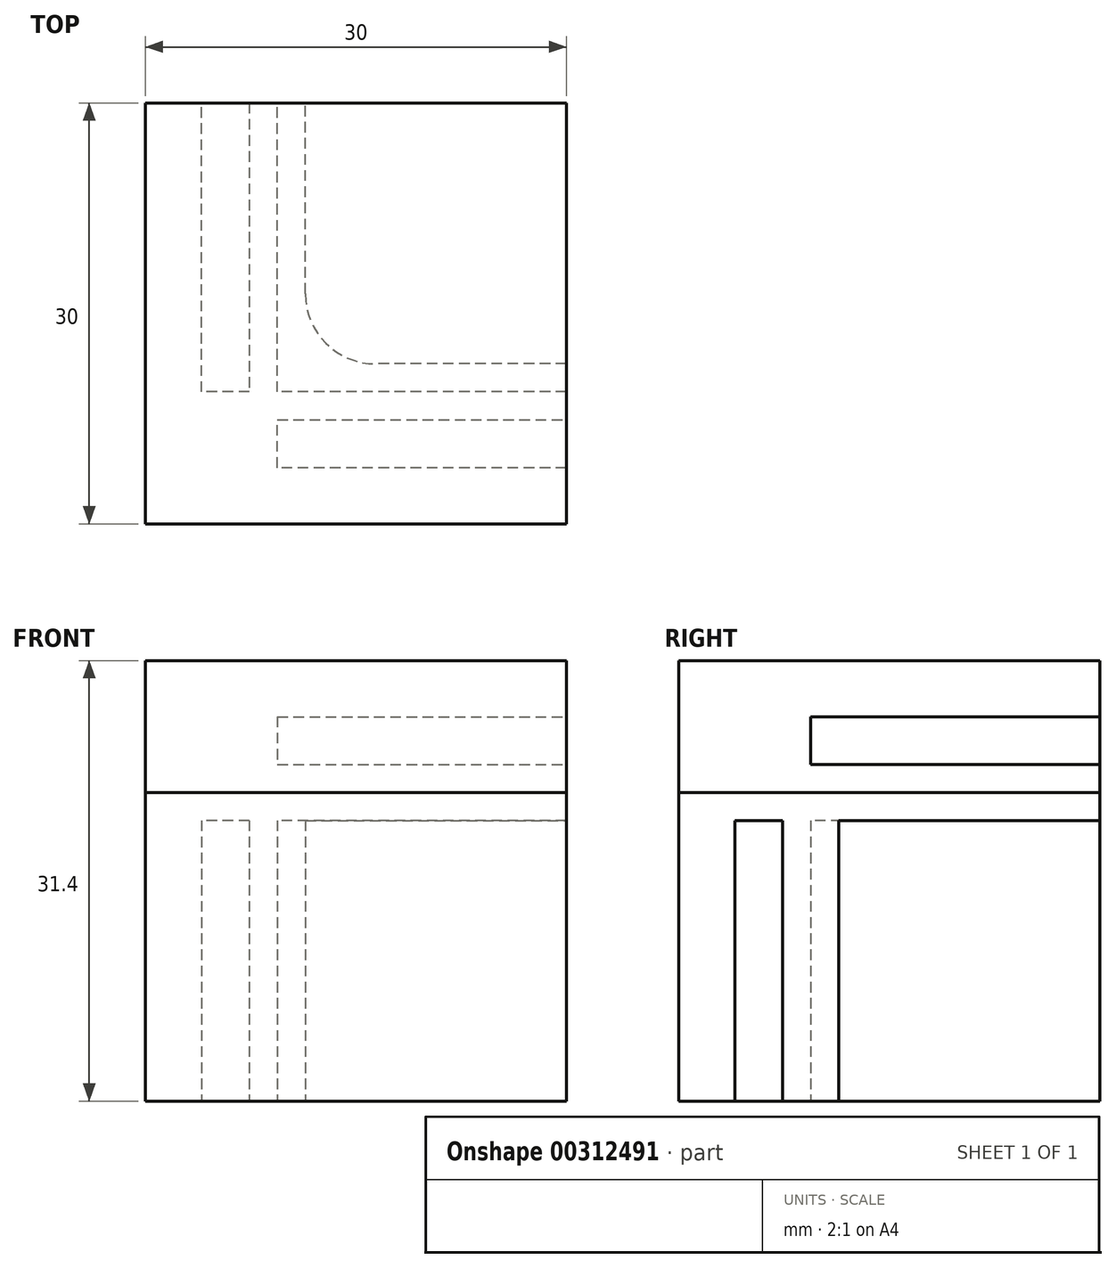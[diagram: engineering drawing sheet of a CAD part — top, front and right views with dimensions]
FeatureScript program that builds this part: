
annotation { "Feature Type Name" : "Feature", "Feature Type Description" : "" }
export const myFeature = defineFeature(function(context is Context, id is Id, definition is map)
    precondition{}
    {
        {
            assignVariable(context, id + "F0", {"name" : "a", "anyValue" : 4});
        }
        {
            assignVariable(context, id + "F1", {"name" : "b", "anyValue" : 3.4});
        }
        {
            assignVariable(context, id + "F2", {"name" : "h", "anyValue" : 30});
        }
        {
            var Q0;
            Q0=qCreatedBy(makeId("Top.planeOp"),FACE);
            var sketch = newSketch(context, id + "F3", { "sketchPlane" : qUnion([Q0])});
            skLineSegment(sketch, "E0", {"start": v(-4, 18.6) * mm, "end": v(-4, -2) * mm});
            skLineSegment(sketch, "E1", {"start": v(-4, -2) * mm, "end": v(-7.4, -2) * mm});
            skLineSegment(sketch, "E2", {"start": v(-7.4, -2) * mm, "end": v(-7.4, 18.6) * mm});
            skLineSegment(sketch, "E3", {"start": v(-7.4, 18.6) * mm, "end": v(-11.4, 18.6) * mm});
            skLineSegment(sketch, "E4", {"start": v(-11.4, 18.6) * mm, "end": v(-11.4, -11.4) * mm});
            skLineSegment(sketch, "E5", {"start": v(-11.4, -11.4) * mm, "end": v(18.6, -11.4) * mm});
            skLineSegment(sketch, "E6", {"start": v(18.6, -11.4) * mm, "end": v(18.6, -7.4) * mm});
            skLineSegment(sketch, "E7", {"start": v(18.6, -7.4) * mm, "end": v(-2, -7.4) * mm});
            skLineSegment(sketch, "E8", {"start": v(-2, -7.4) * mm, "end": v(-2, -4) * mm});
            skLineSegment(sketch, "E9", {"start": v(-2, -4) * mm, "end": v(18.6, -4) * mm});
            skLineSegment(sketch, "E10", {"start": v(18.6, -4) * mm, "end": v(18.6, 0) * mm});
            skLineSegment(sketch, "E11", {"start": v(18.6, 0) * mm, "end": v(0, 0) * mm});
            skLineSegment(sketch, "E12", {"start": v(0, 0) * mm, "end": v(0, 18.6) * mm});
            skLineSegment(sketch, "E13", {"start": v(0, 18.6) * mm, "end": v(-4, 18.6) * mm});
            skLineSegment(sketch, "E14", {"start": v(-4, -2) * mm, "end": v(-2, -2) * mm, "construction": true});
            skLineSegment(sketch, "E15", {"start": v(-2, -4) * mm, "end": v(-2, -2) * mm, "construction": true});
            skSolve(sketch);
        }
        {
            var Q0;
            Q0=makeQuery(id+"F3.imprint","IMPRINT",FACE,{"disambiguationData":[TD([[makeQuery(id+"F3.imprint","IMPRINT",EDGE,{"derivedFrom":sQuery(id+"F3.wireOp",EDGE,"E0")}),1.0]])]});
            extrude(context, id + "F4", {"entities" : qUnion([Q0]), "depth" : (getVariable(context, 'h') - 10) * mm});
        }
        {
            var Q0;
            Q0=makeQuery(id+"F4.opExtrude","CAP_FACE",FACE,{"disambiguationData":[OSD([sQuery(id+"F3.wireOp",EDGE,"E0"),sQuery(id+"F3.wireOp",EDGE,"E1"),sQuery(id+"F3.wireOp",EDGE,"E2"),sQuery(id+"F3.wireOp",EDGE,"E3"),sQuery(id+"F3.wireOp",EDGE,"E4"),sQuery(id+"F3.wireOp",EDGE,"E5"),sQuery(id+"F3.wireOp",EDGE,"E6"),sQuery(id+"F3.wireOp",EDGE,"E7"),sQuery(id+"F3.wireOp",EDGE,"E8"),sQuery(id+"F3.wireOp",EDGE,"E9"),sQuery(id+"F3.wireOp",EDGE,"E10"),sQuery(id+"F3.wireOp",EDGE,"E11"),sQuery(id+"F3.wireOp",EDGE,"E12"),sQuery(id+"F3.wireOp",EDGE,"E13")])],"isStart":false});
            var sketch = newSketch(context, id + "F5", { "sketchPlane" : qUnion([Q0])});
            skLineSegment(sketch, "E16.bottom", {"start": v(-11.4, -11.4) * mm, "end": v(18.6, -11.4) * mm});
            skLineSegment(sketch, "E16.top", {"start": v(-11.4, 18.6) * mm, "end": v(18.6, 18.6) * mm});
            skLineSegment(sketch, "E16.left", {"start": v(-11.4, -11.4) * mm, "end": v(-11.4, 18.6) * mm});
            skLineSegment(sketch, "E16.right", {"start": v(18.6, -11.4) * mm, "end": v(18.6, 18.6) * mm});
            skSolve(sketch);
        }
        {
            var Q0;
            {var subQ1=makeQuery(id+"F4.opExtrude","CAP_EDGE",EDGE,{"disambiguationData":[OSD([sQuery(id+"F3.wireOp",EDGE,"E0")])],"isStart":false});Q0=makeQuery(id+"F5.imprint","IMPRINT",FACE,{"disambiguationData":[TD([[makeQuery(id+"F5.imprint","IMPRINT",EDGE,{"derivedFrom":subQ1}),-1.0]])]});}
            var Q1;
            {var subQ4=sQuery(id+"F5.wireOp",EDGE,"E16.bottom");Q1=makeQuery(id+"F5.imprint","IMPRINT",FACE,{"disambiguationData":[TD([[makeQuery(id+"F5.imprint","IMPRINT",EDGE,{"derivedFrom":subQ4}),1.0]])]});}
            var Q2;
            {var subQ1=makeQuery(id+"F4.opExtrude","CAP_EDGE",EDGE,{"disambiguationData":[OSD([sQuery(id+"F3.wireOp",EDGE,"E7")])],"isStart":false});Q2=makeQuery(id+"F5.imprint","IMPRINT",FACE,{"disambiguationData":[TD([[makeQuery(id+"F5.imprint","IMPRINT",EDGE,{"derivedFrom":subQ1}),-1.0]])]});}
            var Q3;
            {var subQ4=makeQuery(id+"F4.opExtrude","CAP_EDGE",EDGE,{"disambiguationData":[OSD([sQuery(id+"F3.wireOp",EDGE,"E11")])],"isStart":false});Q3=makeQuery(id+"F5.imprint","IMPRINT",FACE,{"disambiguationData":[TD([[makeQuery(id+"F5.imprint","IMPRINT",EDGE,{"derivedFrom":subQ4}),-1.0]])]});}
            extrude(context, id + "F6", {"entities" : qUnion([Q0, Q1, Q2, Q3]), "operationType" : NewBodyOperationType.ADD, "depth" : (getVariable(context, 'a') / 2) * mm});
        }
        {
            var Q0;
            Q0=makeQuery(id+"F6.opExtrude","CAP_FACE",FACE,{"disambiguationData":[OSD([sQuery(id+"F5.wireOp",EDGE,"E16.bottom"),sQuery(id+"F5.wireOp",EDGE,"E16.top"),sQuery(id+"F5.wireOp",EDGE,"E16.left"),sQuery(id+"F5.wireOp",EDGE,"E16.right")])],"isStart":false});
            extrude(context, id + "F7", {"entities" : qUnion([Q0]), "depth" : (getVariable(context, 'a') / 2) * mm});
        }
        {
            var Q0;
            Q0=makeQuery(id+"F7.opExtrude","CAP_FACE",FACE,{"disambiguationData":[OSD([sQuery(id+"F5.wireOp",EDGE,"E16.bottom"),sQuery(id+"F5.wireOp",EDGE,"E16.top"),sQuery(id+"F5.wireOp",EDGE,"E16.left"),sQuery(id+"F5.wireOp",EDGE,"E16.right")])],"isStart":false});
            var sketch = newSketch(context, id + "F8", { "sketchPlane" : qUnion([Q0])});
            skLineSegment(sketch, "E17", {"start": v(-11.4, 18.6) * mm, "end": v(-11.4, -11.4) * mm});
            skLineSegment(sketch, "E18", {"start": v(-11.4, -11.4) * mm, "end": v(18.6, -11.4) * mm});
            skLineSegment(sketch, "E19", {"start": v(18.6, -11.4) * mm, "end": v(18.6, -2) * mm});
            skLineSegment(sketch, "E20", {"start": v(18.6, -2) * mm, "end": v(-2, -2) * mm});
            skLineSegment(sketch, "E21", {"start": v(-2, -2) * mm, "end": v(-2, 18.6) * mm});
            skLineSegment(sketch, "E22", {"start": v(-2, 18.6) * mm, "end": v(-11.4, 18.6) * mm});
            skLineSegment(sketch, "E23", {"start": v(-2, 18.6) * mm, "end": v(-2, -11.4) * mm});
            skPoint(sketch, "E24.0", {"position": v(-2, -2) * mm});
            skSolve(sketch);
        }
        {
            var Q0;
            Q0=makeQuery(id+"F8.imprint","IMPRINT",FACE,{"disambiguationData":[TD([[makeQuery(id+"F8.imprint","IMPRINT",EDGE,{"derivedFrom":sQuery(id+"F8.wireOp",EDGE,"E17")}),1.0]])]});
            var Q1;
            {var subQ0=sQuery(id+"F8.wireOp",EDGE,"E21");Q1=makeQuery(id+"F8.imprint","IMPRINT",FACE,{"disambiguationData":[TD([[makeQuery(id+"F8.imprint","IMPRINT",EDGE,{"derivedFrom":subQ0}),1.0]])]});}
            var Q2;
            {var subQ0=sQuery(id+"F8.wireOp",EDGE,"E19");Q2=makeQuery(id+"F8.imprint","IMPRINT",FACE,{"disambiguationData":[TD([[makeQuery(id+"F8.imprint","IMPRINT",EDGE,{"derivedFrom":subQ0}),1.0]])]});}
            extrude(context, id + "F9", {"entities" : qUnion([Q0, Q1, Q2]), "operationType" : NewBodyOperationType.ADD, "depth" : (getVariable(context, 'b')) * mm});
        }
        {
            var Q0;
            Q0=makeQuery(id+"F9.opExtrude","CAP_FACE",FACE,{"disambiguationData":[OSD([sQuery(id+"F5.wireOp",EDGE,"E16.top"),sQuery(id+"F8.wireOp",EDGE,"E17"),sQuery(id+"F8.wireOp",EDGE,"E18"),sQuery(id+"F8.wireOp",EDGE,"E19"),sQuery(id+"F8.wireOp",EDGE,"E20"),sQuery(id+"F8.wireOp",EDGE,"E21"),sQuery(id+"F8.wireOp",EDGE,"E23")])],"isStart":false});
            var sketch = newSketch(context, id + "F10", { "sketchPlane" : qUnion([Q0])});
            skPoint(sketch, "E25.0", {"position": v(18.6, 18.6) * mm});
            skLineSegment(sketch, "E26.bottom", {"start": v(-11.4, -11.4) * mm, "end": v(18.6, -11.4) * mm});
            skLineSegment(sketch, "E26.top", {"start": v(-11.4, 18.6) * mm, "end": v(18.6, 18.6) * mm});
            skLineSegment(sketch, "E26.left", {"start": v(-11.4, -11.4) * mm, "end": v(-11.4, 18.6) * mm});
            skLineSegment(sketch, "E26.right", {"start": v(18.6, -11.4) * mm, "end": v(18.6, 18.6) * mm});
            skSolve(sketch);
        }
        {
            var Q0;
            Q0=qSketchRegion(id+"F10",true);
            extrude(context, id + "F11", {"entities" : qUnion([Q0]), "operationType" : NewBodyOperationType.ADD, "depth" : (getVariable(context, 'a')) * mm});
        }
        {
            var Q0;
            Q0=makeQuery(id+"F4.opExtrude","SWEPT_EDGE",EDGE,{"disambiguationData":[OSD([sQuery(id+"F3.wireOp",EDGE,"E11"),sQuery(id+"F3.wireOp",EDGE,"E12")])]});
            var Q1;
            Q1=makeQuery(id+"F4.opExtrude","CAP_EDGE",EDGE,{"disambiguationData":[OSD([sQuery(id+"F3.wireOp",EDGE,"E12")])],"isStart":false});
            var Q2;
            Q2=makeQuery(id+"F4.opExtrude","CAP_EDGE",EDGE,{"disambiguationData":[OSD([sQuery(id+"F3.wireOp",EDGE,"E11")])],"isStart":false});
            fillet(context, id + "F12", {"entities" : qUnion([Q0, Q1, Q2]), "radius" : 5 * mm, "tangentPropagation" : true, "allowEdgeOverflow" : false});
        }
    });
